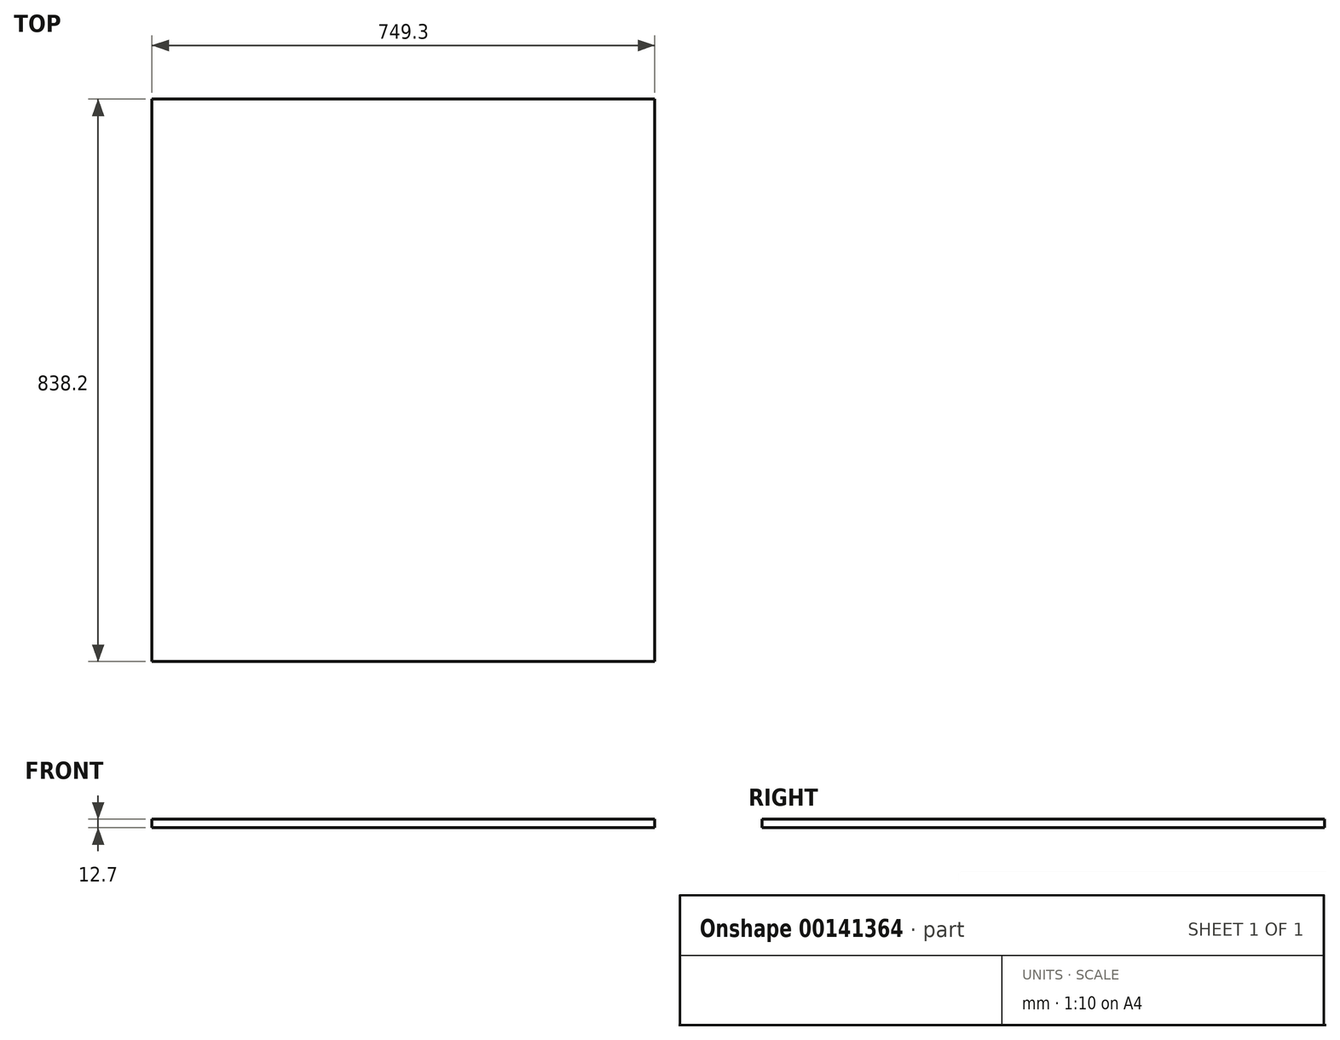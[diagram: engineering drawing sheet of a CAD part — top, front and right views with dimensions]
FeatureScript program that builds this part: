
annotation { "Feature Type Name" : "Feature", "Feature Type Description" : "" }
export const myFeature = defineFeature(function(context is Context, id is Id, definition is map)
    precondition{}
    {
        {
            var Q0;
            Q0=qCreatedBy(makeId("Top.planeOp"),FACE);
            var sketch = newSketch(context, id + "F0", { "sketchPlane" : qUnion([Q0])});
            skLineSegment(sketch, "E0.bottom", {"start": v(-1246.62, 803.73) * mm, "end": v(-497.32, 803.73) * mm});
            skLineSegment(sketch, "E0.top", {"start": v(-1246.62, -34.47) * mm, "end": v(-497.32, -34.47) * mm});
            skLineSegment(sketch, "E0.left", {"start": v(-1246.62, 803.73) * mm, "end": v(-1246.62, -34.47) * mm});
            skLineSegment(sketch, "E0.right", {"start": v(-497.32, 803.73) * mm, "end": v(-497.32, -34.47) * mm});
            skSolve(sketch);
        }
        {
            var Q0;
            Q0=qSketchRegion(id+"F0",true);
            extrude(context, id + "F1", {"entities" : qUnion([Q0]), "depth" : 12.7 * mm});
        }
    });
